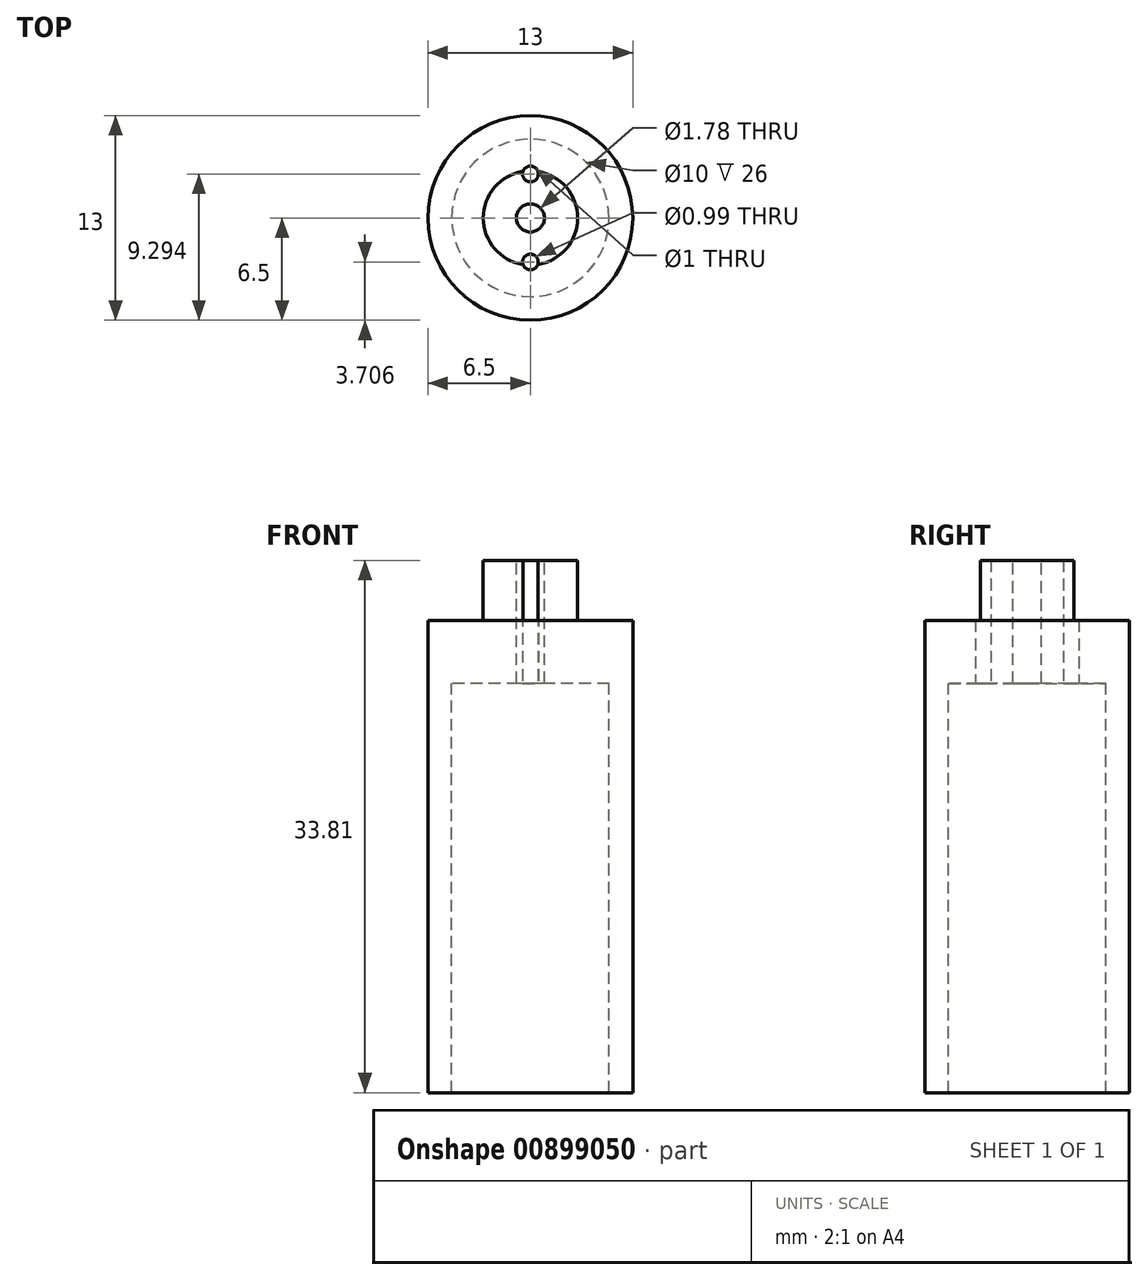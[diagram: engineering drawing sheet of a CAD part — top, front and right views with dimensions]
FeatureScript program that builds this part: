
annotation { "Feature Type Name" : "Feature", "Feature Type Description" : "" }
export const myFeature = defineFeature(function(context is Context, id is Id, definition is map)
    precondition{}
    {
        {
            var Q0;
            Q0=qCreatedBy(makeId("Right.planeOp"),FACE);
            var sketch = newSketch(context, id + "F0", { "sketchPlane" : qUnion([Q0])});
            skLineSegment(sketch, "E0", {"start": v(0, 5.14) * mm, "end": v(0, -5.15) * mm, "construction": true});
            skLineSegment(sketch, "E1", {"start": v(6.5, 0) * mm, "end": v(6.5, 30) * mm});
            skLineSegment(sketch, "E2", {"start": v(6.5, 30) * mm, "end": v(3, 30) * mm});
            skLineSegment(sketch, "E3", {"start": v(3, 30) * mm, "end": v(3, 33.81) * mm});
            skLineSegment(sketch, "E4", {"start": v(3, 33.81) * mm, "end": v(0.89, 33.81) * mm});
            skLineSegment(sketch, "E5", {"start": v(0.89, 33.81) * mm, "end": v(0.89, 26) * mm});
            skLineSegment(sketch, "E6", {"start": v(5, 0) * mm, "end": v(6.5, 0) * mm});
            skLineSegment(sketch, "E7", {"start": v(0.89, 26) * mm, "end": v(5, 26) * mm});
            skLineSegment(sketch, "E8", {"start": v(5, 26) * mm, "end": v(5, 0) * mm});
            skPoint(sketch, "E9.orphan", {"position": v(0.89, 0) * mm});
            skSolve(sketch);
        }
        {
            var Q0;
            Q0=makeQuery(id+"F0.imprint","IMPRINT",FACE,{"disambiguationData":[TD([[makeQuery(id+"F0.imprint","IMPRINT",EDGE,{"derivedFrom":sQuery(id+"F0.wireOp",EDGE,"E1")}),1.0]])]});
            var Q1;
            Q1=sQuery(id+"F0.wireOp",EDGE,"E0");
            revolve(context, id + "F1", {"surfaceOperationType" : NewSurfaceOperationType.NEW, "entities" : qUnion([Q0]), "axis" : qUnion([Q1]), "revolveType" : RevolveType.FULL});
        }
        {
            var Q0;
            Q0=makeQuery(id+"F1.opRevolve","SWEPT_FACE",FACE,{"disambiguationData":[OSD([sQuery(id+"F0.wireOp",EDGE,"E7")])]});
            var sketch = newSketch(context, id + "F2", { "sketchPlane" : qUnion([Q0])});
            skCircle(sketch, "E10", {"center": v(0, -2.8) * mm, "radius": 0.5 * mm});
            skPoint(sketch, "E11.0", {"position": v(0, 0) * mm});
            skCircle(sketch, "E12", {"center": v(0, 2.8) * mm, "radius": 0.5 * mm});
            skSolve(sketch);
        }
        {
            var Q0;
            Q0=makeQuery(id+"F2.imprint","IMPRINT",FACE,{"disambiguationData":[TD([[makeQuery(id+"F2.imprint","IMPRINT",EDGE,{"derivedFrom":sQuery(id+"F2.wireOp",EDGE,"E10")}),1.0]])]});
            var Q1;
            Q1=makeQuery(id+"F2.imprint","IMPRINT",FACE,{"disambiguationData":[TD([[makeQuery(id+"F2.imprint","IMPRINT",EDGE,{"derivedFrom":sQuery(id+"F2.wireOp",EDGE,"E12")}),1.0]])]});
            extrude(context, id + "F3", {"entities" : qUnion([Q0, Q1]), "operationType" : NewBodyOperationType.REMOVE, "oppositeDirection" : true, "depth" : 25.4 * mm, "offsetDistance" : 25.4 * mm});
        }
    });
